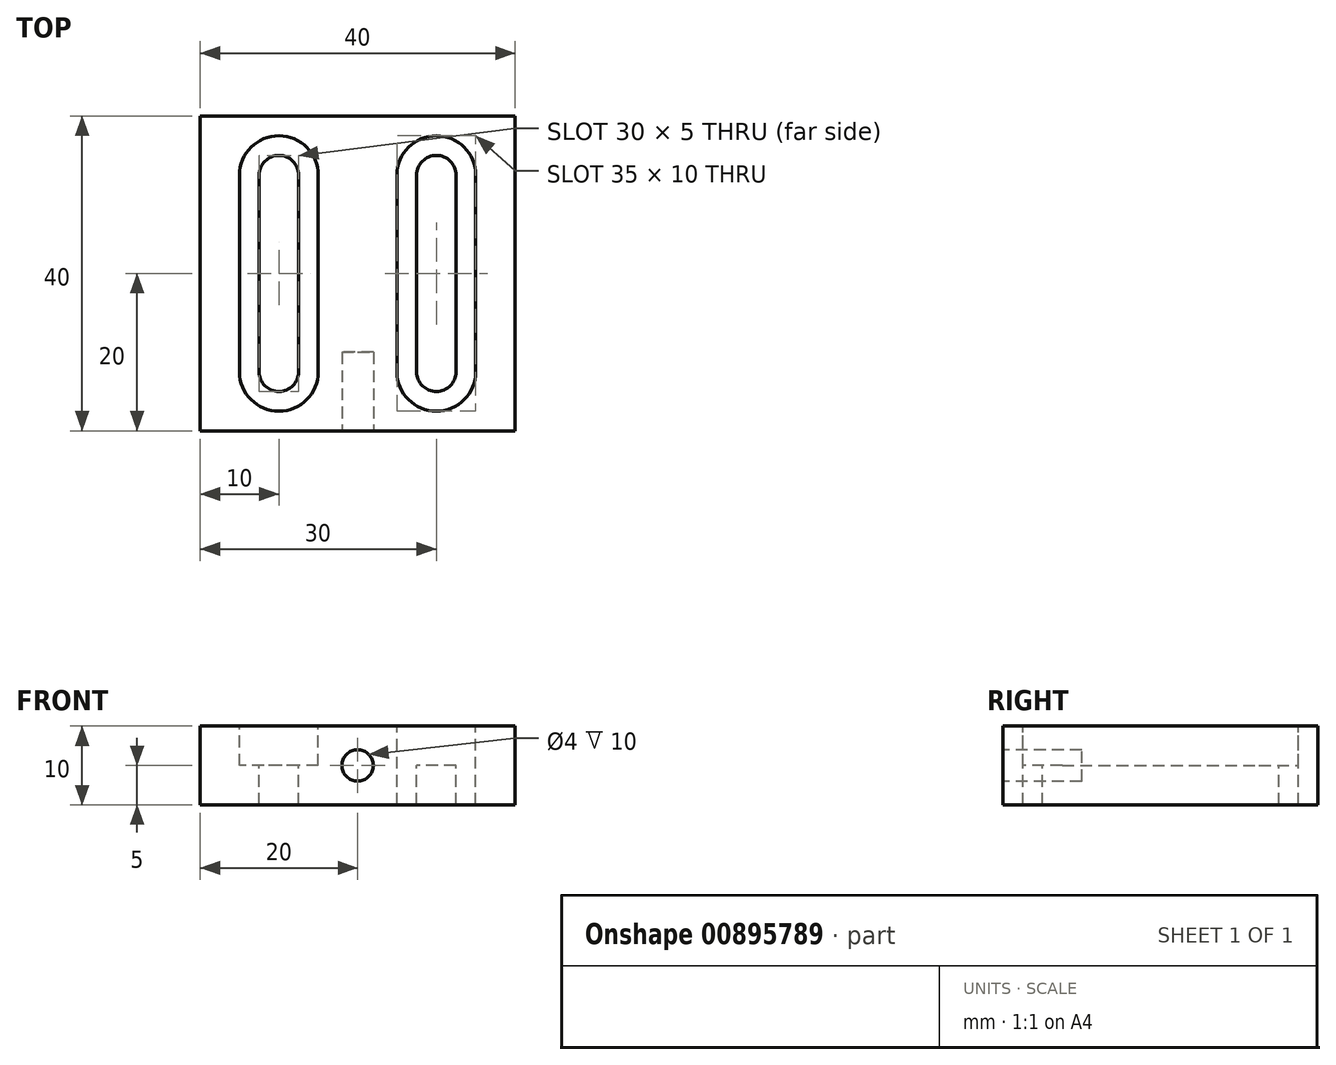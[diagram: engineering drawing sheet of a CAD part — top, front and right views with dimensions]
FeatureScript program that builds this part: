
annotation { "Feature Type Name" : "Feature", "Feature Type Description" : "" }
export const myFeature = defineFeature(function(context is Context, id is Id, definition is map)
    precondition{}
    {
        {
            var Q0;
            Q0=qCreatedBy(makeId("Top.planeOp"),FACE);
            var sketch = newSketch(context, id + "F0", { "sketchPlane" : qUnion([Q0])});
            skLineSegment(sketch, "E0.bottom", {"start": v(-20, 20) * mm, "end": v(20, 20) * mm});
            skLineSegment(sketch, "E0.top", {"start": v(-20, -20) * mm, "end": v(20, -20) * mm});
            skLineSegment(sketch, "E0.left", {"start": v(-20, 20) * mm, "end": v(-20, -20) * mm});
            skLineSegment(sketch, "E0.right", {"start": v(20, 20) * mm, "end": v(20, -20) * mm});
            skPoint(sketch, "E0.middle", {"position": v(0, 0) * mm});
            skLineSegment(sketch, "E1.bottom", {"start": v(-10, 15) * mm, "end": v(-10, 15) * mm});
            skLineSegment(sketch, "E1.top", {"start": v(-10, -15) * mm, "end": v(-10, -15) * mm});
            skLineSegment(sketch, "E1.left", {"start": v(-7.5, 12.5) * mm, "end": v(-7.5, -12.5) * mm});
            skLineSegment(sketch, "E1.right", {"start": v(-12.5, 12.5) * mm, "end": v(-12.5, -12.5) * mm});
            skPoint(sketch, "E1.middle", {"position": v(-10, 0) * mm});
            skPoint(sketch, "E2.visualSharp", {"position": v(-12.5, 15) * mm});
            skArc(sketch, "E2.filletArc", {"start": v(-10, 15) * mm, "mid": v(-11.77, 14.27) * mm, "end": v(-12.5, 12.5) * mm});
            skPoint(sketch, "E3.visualSharp", {"position": v(-7.5, 15) * mm});
            skArc(sketch, "E3.filletArc", {"start": v(-7.5, 12.5) * mm, "mid": v(-8.23, 14.27) * mm, "end": v(-10, 15) * mm});
            skPoint(sketch, "E4.visualSharp", {"position": v(-7.5, -15) * mm});
            skArc(sketch, "E4.filletArc", {"start": v(-10, -15) * mm, "mid": v(-8.23, -14.27) * mm, "end": v(-7.5, -12.5) * mm});
            skPoint(sketch, "E5.visualSharp", {"position": v(-12.5, -15) * mm});
            skArc(sketch, "E5.filletArc", {"start": v(-12.5, -12.5) * mm, "mid": v(-11.77, -14.27) * mm, "end": v(-10, -15) * mm});
            skLineSegment(sketch, "E6.bottom", {"start": v(-10, 17.5) * mm, "end": v(-10, 17.5) * mm});
            skLineSegment(sketch, "E6.top", {"start": v(-10, -17.5) * mm, "end": v(-10, -17.5) * mm});
            skLineSegment(sketch, "E6.left", {"start": v(-15, 12.5) * mm, "end": v(-15, -12.5) * mm});
            skLineSegment(sketch, "E6.right", {"start": v(-5, 12.5) * mm, "end": v(-5, -12.5) * mm});
            skPoint(sketch, "E7.visualSharp", {"position": v(-15, 17.5) * mm});
            skArc(sketch, "E7.filletArc", {"start": v(-10, 17.5) * mm, "mid": v(-13.54, 16.04) * mm, "end": v(-15, 12.5) * mm});
            skPoint(sketch, "E8.visualSharp", {"position": v(-5, 17.5) * mm});
            skArc(sketch, "E8.filletArc", {"start": v(-5, 12.5) * mm, "mid": v(-6.46, 16.04) * mm, "end": v(-10, 17.5) * mm});
            skPoint(sketch, "E9.visualSharp", {"position": v(-5, -17.5) * mm});
            skArc(sketch, "E9.filletArc", {"start": v(-10, -17.5) * mm, "mid": v(-6.46, -16.04) * mm, "end": v(-5, -12.5) * mm});
            skPoint(sketch, "E10.visualSharp", {"position": v(-15, -17.5) * mm});
            skArc(sketch, "E10.filletArc", {"start": v(-15, -12.5) * mm, "mid": v(-13.54, -16.04) * mm, "end": v(-10, -17.5) * mm});
            skArc(sketch, "E11.MirrorCS", {"start": v(7.5, 12.5) * mm, "mid": v(8.23, 14.27) * mm, "end": v(10, 15) * mm});
            skArc(sketch, "E12.MirrorCS", {"start": v(10, -15) * mm, "mid": v(8.23, -14.27) * mm, "end": v(7.5, -12.5) * mm});
            skArc(sketch, "E13.MirrorCS", {"start": v(5, 12.5) * mm, "mid": v(6.46, 16.04) * mm, "end": v(10, 17.5) * mm});
            skArc(sketch, "E14.MirrorCS", {"start": v(12.5, -12.5) * mm, "mid": v(11.77, -14.27) * mm, "end": v(10, -15) * mm});
            skArc(sketch, "E15.MirrorCS", {"start": v(10, -17.5) * mm, "mid": v(6.46, -16.04) * mm, "end": v(5, -12.5) * mm});
            skArc(sketch, "E16.MirrorCS", {"start": v(15, -12.5) * mm, "mid": v(13.54, -16.04) * mm, "end": v(10, -17.5) * mm});
            skArc(sketch, "E17.MirrorCS", {"start": v(10, 15) * mm, "mid": v(11.77, 14.27) * mm, "end": v(12.5, 12.5) * mm});
            skPoint(sketch, "E18.MirrorP", {"position": v(10, 0) * mm});
            skArc(sketch, "E19.MirrorCS", {"start": v(10, 17.5) * mm, "mid": v(13.54, 16.04) * mm, "end": v(15, 12.5) * mm});
            skPoint(sketch, "E20.MirrorP", {"position": v(5, -17.5) * mm});
            skLineSegment(sketch, "E21.MirrorCS", {"start": v(5, 12.5) * mm, "end": v(5, -12.5) * mm});
            skLineSegment(sketch, "E22.MirrorCS", {"start": v(15, 12.5) * mm, "end": v(15, -12.5) * mm});
            skPoint(sketch, "E23.MirrorP", {"position": v(7.5, -15) * mm});
            skLineSegment(sketch, "E24.MirrorCS", {"start": v(10, -15) * mm, "end": v(10, -15) * mm});
            skPoint(sketch, "E25.MirrorP", {"position": v(5, 17.5) * mm});
            skPoint(sketch, "E26.MirrorP", {"position": v(15, 17.5) * mm});
            skLineSegment(sketch, "E27.MirrorCS", {"start": v(10, 17.5) * mm, "end": v(10, 17.5) * mm});
            skPoint(sketch, "E28.MirrorP", {"position": v(12.5, -15) * mm});
            skPoint(sketch, "E29.MirrorP", {"position": v(12.5, 15) * mm});
            skLineSegment(sketch, "E30.MirrorCS", {"start": v(7.5, 12.5) * mm, "end": v(7.5, -12.5) * mm});
            skLineSegment(sketch, "E31.MirrorCS", {"start": v(12.5, 12.5) * mm, "end": v(12.5, -12.5) * mm});
            skLineSegment(sketch, "E32.MirrorCS", {"start": v(10, -17.5) * mm, "end": v(10, -17.5) * mm});
            skPoint(sketch, "E33.MirrorP", {"position": v(15, -17.5) * mm});
            skPoint(sketch, "E34.MirrorP", {"position": v(7.5, 15) * mm});
            skLineSegment(sketch, "E35.MirrorCS", {"start": v(10, 15) * mm, "end": v(10, 15) * mm});
            skSolve(sketch);
        }
        {
            var Q0;
            Q0=qSketchRegion(id+"F0",true);
            var Q1;
            Q1=makeQuery(id+"F0.imprint","IMPRINT",FACE,{"disambiguationData":[TD([[makeQuery(id+"F0.imprint","IMPRINT",EDGE,{"derivedFrom":sQuery(id+"F0.wireOp",EDGE,"E1.left")}),1.0]])]});
            var Q2;
            Q2=makeQuery(id+"F0.imprint","IMPRINT",FACE,{"disambiguationData":[TD([[makeQuery(id+"F0.imprint","IMPRINT",EDGE,{"derivedFrom":sQuery(id+"F0.wireOp",EDGE,"E11.MirrorCS")}),1.0]])]});
            extrude(context, id + "F1", {"entities" : qUnion([Q0, Q1, Q2]), "oppositeDirection" : true, "depth" : 10 * mm, "offsetDistance" : 25 * mm});
        }
        {
            var Q0;
            Q0=makeQuery(id+"F0.imprint","IMPRINT",FACE,{"disambiguationData":[TD([[makeQuery(id+"F0.imprint","IMPRINT",EDGE,{"derivedFrom":sQuery(id+"F0.wireOp",EDGE,"E1.left")}),-1.0]])]});
            var Q1;
            Q1=makeQuery(id+"F0.imprint","IMPRINT",FACE,{"disambiguationData":[TD([[makeQuery(id+"F0.imprint","IMPRINT",EDGE,{"derivedFrom":sQuery(id+"F0.wireOp",EDGE,"E11.MirrorCS")}),-1.0]])]});
            var Q2;
            Q2=makeQuery(id+"F0.imprint","IMPRINT",FACE,{"disambiguationData":[TD([[makeQuery(id+"F0.imprint","IMPRINT",EDGE,{"derivedFrom":sQuery(id+"F0.wireOp",EDGE,"E11.MirrorCS")}),1.0]])]});
            var Q3;
            Q3=makeQuery(id+"F0.imprint","IMPRINT",FACE,{"disambiguationData":[TD([[makeQuery(id+"F0.imprint","IMPRINT",EDGE,{"derivedFrom":sQuery(id+"F0.wireOp",EDGE,"E1.left")}),1.0]])]});
            extrude(context, id + "F2", {"entities" : qUnion([Q0, Q1, Q2, Q3]), "operationType" : NewBodyOperationType.REMOVE, "oppositeDirection" : true, "depth" : 5 * mm, "offsetDistance" : 25 * mm});
        }
        {
            var Q0;
            Q0=makeQuery(id+"F1.opExtrude","SWEPT_FACE",FACE,{"disambiguationData":[OSD([sQuery(id+"F0.wireOp",EDGE,"E0.top")])]});
            var sketch = newSketch(context, id + "F3", { "sketchPlane" : qUnion([Q0])});
            skCircle(sketch, "E36", {"center": v(0, -5) * mm, "radius": 2 * mm});
            skPoint(sketch, "E36.centerSnap0", {"position": v(-20, -5) * mm});
            skSolve(sketch);
        }
        {
            var Q0;
            Q0=qSketchRegion(id+"F3",true);
            extrude(context, id + "F4", {"entities" : qUnion([Q0]), "operationType" : NewBodyOperationType.REMOVE, "oppositeDirection" : true, "depth" : 10 * mm, "offsetDistance" : 25 * mm});
        }
    });
